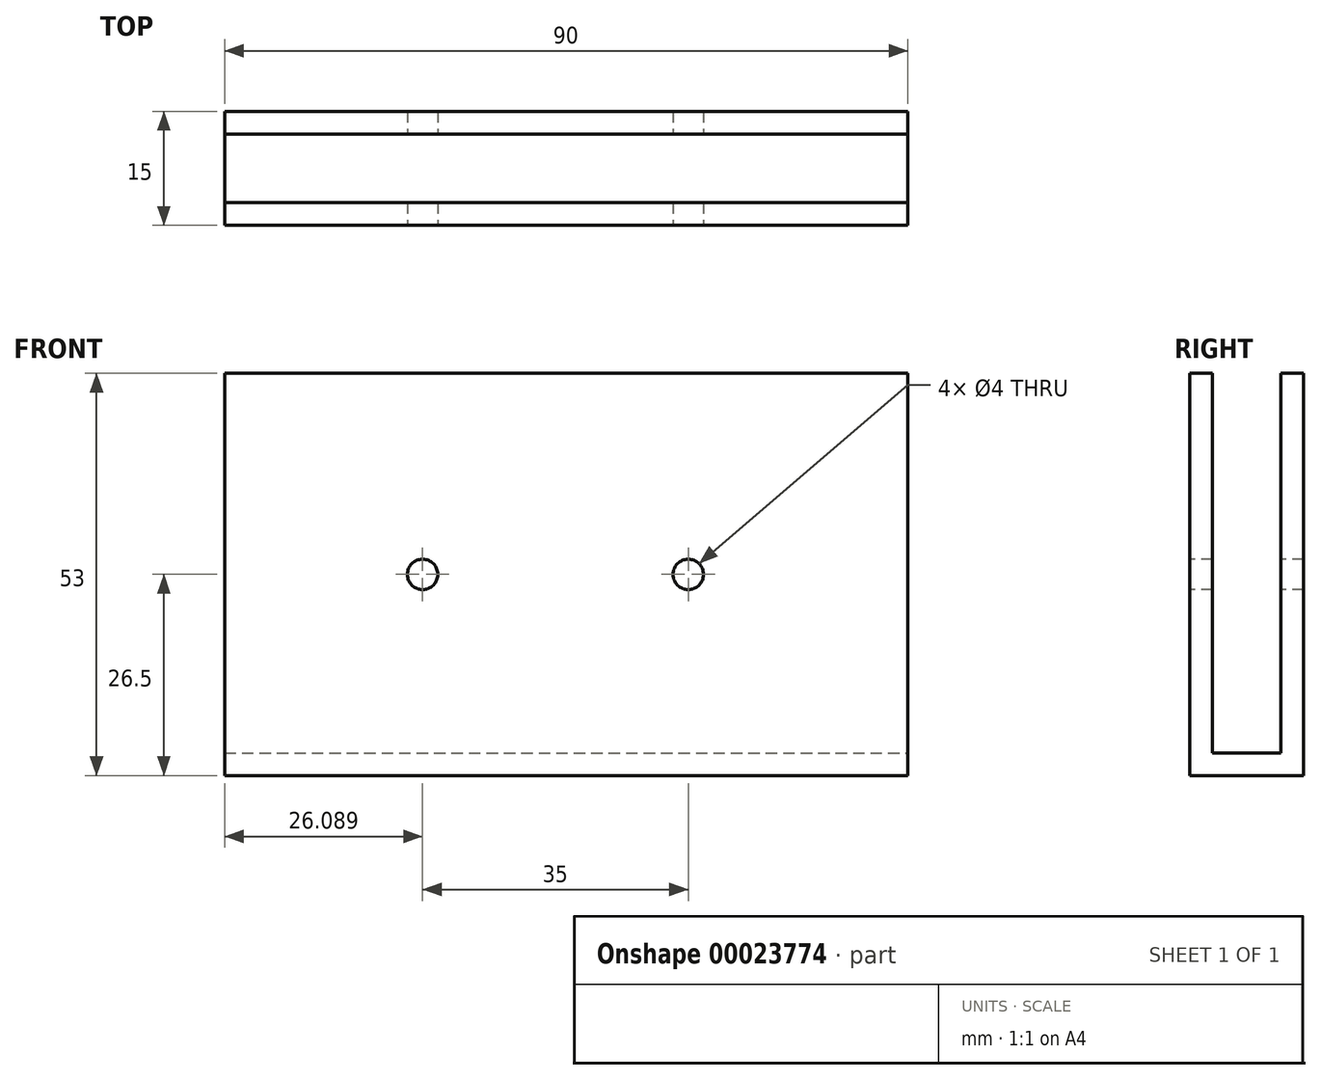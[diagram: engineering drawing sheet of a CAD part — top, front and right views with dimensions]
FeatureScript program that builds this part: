
annotation { "Feature Type Name" : "Feature", "Feature Type Description" : "" }
export const myFeature = defineFeature(function(context is Context, id is Id, definition is map)
    precondition{}
    {
        {
            var Q0;
            Q0=qCreatedBy(makeId("Top.planeOp"),FACE);
            var sketch = newSketch(context, id + "F0", { "sketchPlane" : qUnion([Q0])});
            skLineSegment(sketch, "E0.bottom", {"start": v(-4.29, 7.51) * mm, "end": v(85.71, 7.51) * mm});
            skLineSegment(sketch, "E0.top", {"start": v(-4.29, -7.49) * mm, "end": v(85.71, -7.49) * mm});
            skLineSegment(sketch, "E0.left", {"start": v(-4.29, 7.51) * mm, "end": v(-4.29, -7.49) * mm});
            skLineSegment(sketch, "E0.right", {"start": v(85.71, 7.51) * mm, "end": v(85.71, -7.49) * mm});
            skSolve(sketch);
        }
        {
            var Q0;
            Q0 = qSketchRegion(id + "F0", true);
            extrude(context, id + "F1", {"entities" : qUnion([Q0]), "depth" : 3 * mm});
        }
        {
            var Q0;
            Q0=makeQuery(id+"F1.opExtrude","CAP_FACE",FACE,{"disambiguationData":[OSD([sQuery(id+"F0.wireOp",EDGE,"E0.bottom"),sQuery(id+"F0.wireOp",EDGE,"E0.top"),sQuery(id+"F0.wireOp",EDGE,"E0.left"),sQuery(id+"F0.wireOp",EDGE,"E0.right")])],"isStart":false});
            var sketch = newSketch(context, id + "F2", { "sketchPlane" : qUnion([Q0])});
            skLineSegment(sketch, "E1.bottom", {"start": v(-4.29, 7.51) * mm, "end": v(85.71, 7.51) * mm});
            skLineSegment(sketch, "E1.top", {"start": v(-4.29, 4.51) * mm, "end": v(85.71, 4.51) * mm});
            skLineSegment(sketch, "E1.left", {"start": v(-4.29, 7.51) * mm, "end": v(-4.29, 4.51) * mm});
            skLineSegment(sketch, "E1.right", {"start": v(85.71, 7.51) * mm, "end": v(85.71, 4.51) * mm});
            skLineSegment(sketch, "E2.bottom", {"start": v(-4.29, -7.49) * mm, "end": v(85.71, -7.49) * mm});
            skLineSegment(sketch, "E2.top", {"start": v(-4.29, -4.49) * mm, "end": v(85.71, -4.49) * mm});
            skLineSegment(sketch, "E2.left", {"start": v(-4.29, -7.49) * mm, "end": v(-4.29, -4.49) * mm});
            skLineSegment(sketch, "E2.right", {"start": v(85.71, -7.49) * mm, "end": v(85.71, -4.49) * mm});
            skSolve(sketch);
        }
        {
            var Q0;
            Q0 = qSketchRegion(id + "F2", true);
            extrude(context, id + "F3", {"entities" : qUnion([Q0]), "operationType" : NewBodyOperationType.ADD, "depth" : 50 * mm});
        }
        {
            var Q0;
            Q0=makeQuery(id+"F3.boolean.opBoolean","MERGE",FACE,{"derivedFrom":[makeQuery(id+"F1.opExtrude","SWEPT_FACE",FACE,{"disambiguationData":[OSD([sQuery(id+"F0.wireOp",EDGE,"E0.top")])]}),makeQuery(id+"F3.opExtrude","SWEPT_FACE",FACE,{"disambiguationData":[OSD([sQuery(id+"F2.wireOp",EDGE,"E2.bottom")])]})]});
            var sketch = newSketch(context, id + "F4", { "sketchPlane" : qUnion([Q0])});
            skPoint(sketch, "E3", {"position": v(85.71, 26.5) * mm});
            skPoint(sketch, "E4", {"position": v(56.8, 26.5) * mm});
            skPoint(sketch, "E5", {"position": v(21.8, 26.5) * mm});
            skCircle(sketch, "E6", {"center": v(21.8, 26.5) * mm, "radius": 2 * mm});
            skCircle(sketch, "E7", {"center": v(56.8, 26.5) * mm, "radius": 2 * mm});
            skSolve(sketch);
        }
        {
            var Q0;
            Q0 = qSketchRegion(id + "F4", true);
            extrude(context, id + "F5", {"entities" : qUnion([Q0]), "operationType" : NewBodyOperationType.REMOVE, "endBound" : BoundingType.THROUGH_ALL, "oppositeDirection" : true, "depth" : 25 * mm});
        }
    });
